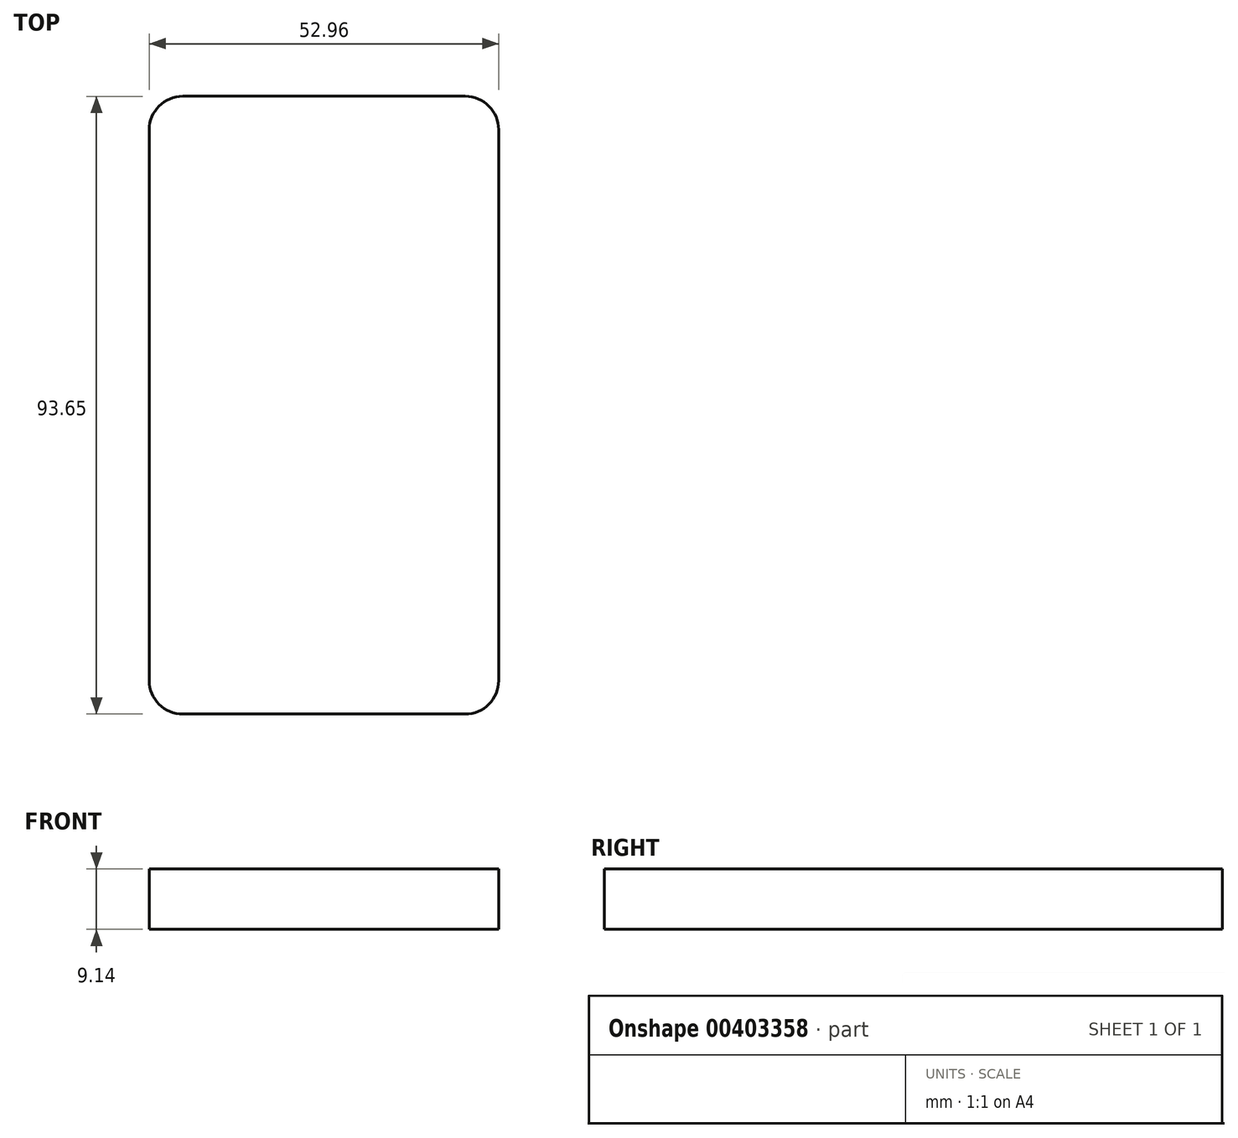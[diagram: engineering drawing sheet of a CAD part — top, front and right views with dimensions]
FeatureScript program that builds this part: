
annotation { "Feature Type Name" : "Feature", "Feature Type Description" : "" }
export const myFeature = defineFeature(function(context is Context, id is Id, definition is map)
    precondition{}
    {
        {
            var Q0;
            Q0=qCreatedBy(makeId("Top.planeOp"),FACE);
            var sketch = newSketch(context, id + "F0", { "sketchPlane" : qUnion([Q0])});
            skLineSegment(sketch, "E0.bottom", {"start": v(-24.8, -34.86) * mm, "end": v(28.17, -34.86) * mm});
            skLineSegment(sketch, "E0.top", {"start": v(-24.8, 58.8) * mm, "end": v(28.17, 58.8) * mm});
            skLineSegment(sketch, "E0.left", {"start": v(-24.8, -34.86) * mm, "end": v(-24.8, 58.8) * mm});
            skLineSegment(sketch, "E0.right", {"start": v(28.17, -34.86) * mm, "end": v(28.17, 58.8) * mm});
            skSolve(sketch);
        }
        {
            var Q0;
            Q0=makeQuery(id+"F0.imprint","IMPRINT",FACE,{"disambiguationData":[TD([[makeQuery(id+"F0.imprint","IMPRINT",EDGE,{"derivedFrom":sQuery(id+"F0.wireOp",EDGE,"E0.bottom")}),1.0]])]});
            extrude(context, id + "F1", {"entities" : qUnion([Q0]), "depth" : 9.14 * mm});
        }
        {
            var Q0;
            Q0=makeQuery(id+"F1.opExtrude","SWEPT_EDGE",EDGE,{"disambiguationData":[OSD([sQuery(id+"F0.wireOp",EDGE,"E0.bottom"),sQuery(id+"F0.wireOp",EDGE,"E0.right")])]});
            var Q1;
            Q1=makeQuery(id+"F1.opExtrude","SWEPT_EDGE",EDGE,{"disambiguationData":[OSD([sQuery(id+"F0.wireOp",EDGE,"E0.bottom"),sQuery(id+"F0.wireOp",EDGE,"E0.left")])]});
            var Q2;
            Q2=makeQuery(id+"F1.opExtrude","SWEPT_EDGE",EDGE,{"disambiguationData":[OSD([sQuery(id+"F0.wireOp",EDGE,"E0.top"),sQuery(id+"F0.wireOp",EDGE,"E0.right")])]});
            var Q3;
            Q3=makeQuery(id+"F1.opExtrude","SWEPT_EDGE",EDGE,{"disambiguationData":[OSD([sQuery(id+"F0.wireOp",EDGE,"E0.top"),sQuery(id+"F0.wireOp",EDGE,"E0.left")])]});
            fillet(context, id + "F2", {"entities" : qUnion([Q0, Q1, Q2, Q3]), "radius" : 5.08 * mm, "tangentPropagation" : true, "allowEdgeOverflow" : false});
        }
    });
